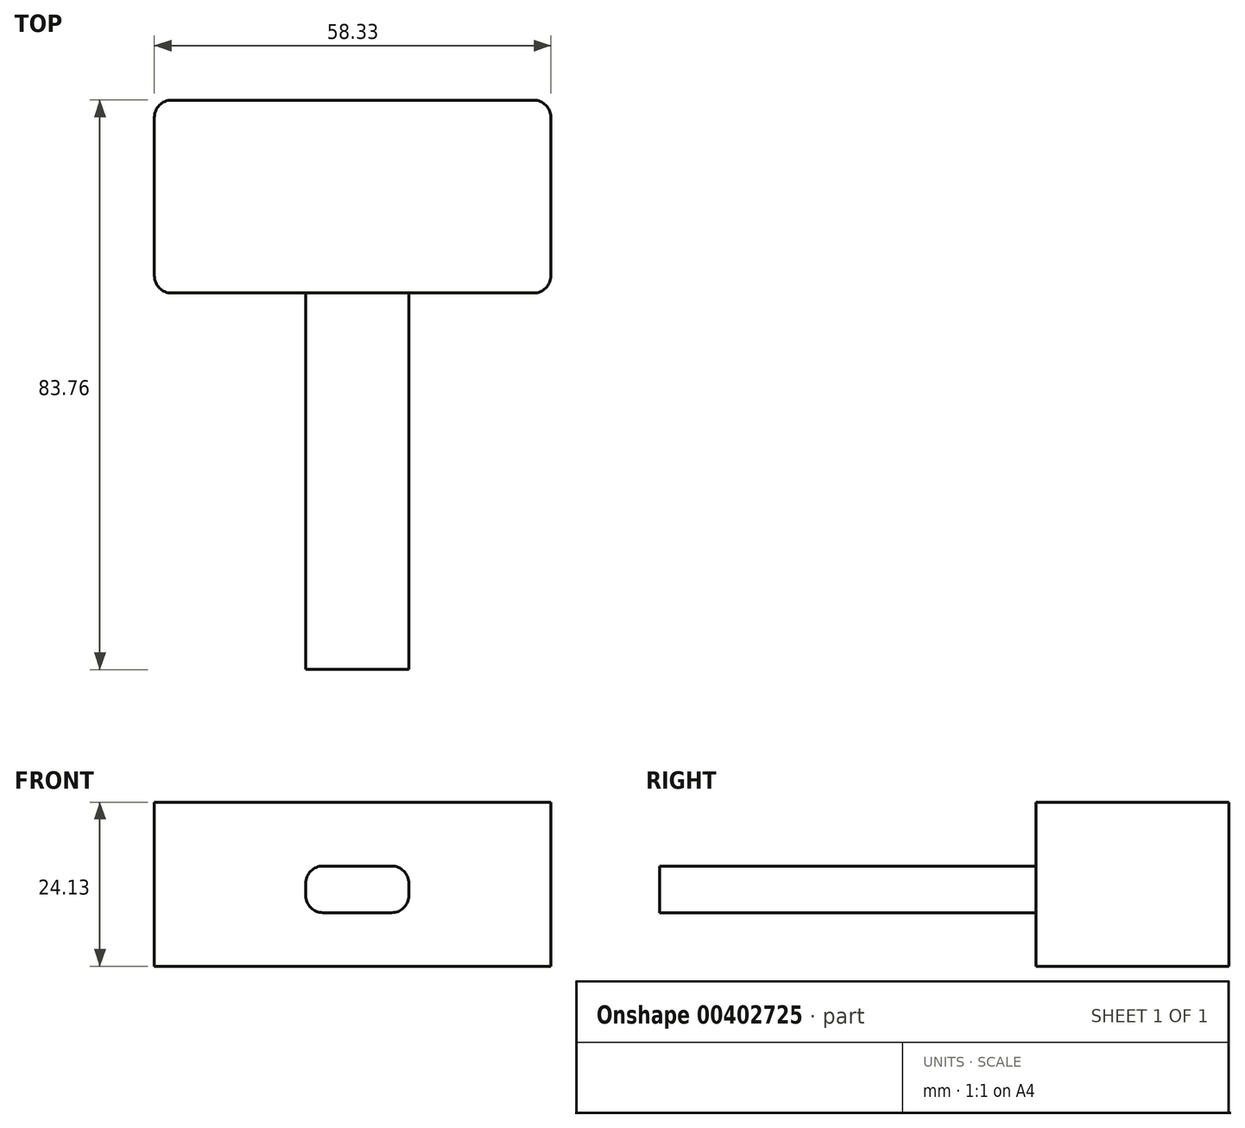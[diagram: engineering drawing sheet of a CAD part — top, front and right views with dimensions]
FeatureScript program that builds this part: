
annotation { "Feature Type Name" : "Feature", "Feature Type Description" : "" }
export const myFeature = defineFeature(function(context is Context, id is Id, definition is map)
    precondition{}
    {
        {
            var Q0;
            Q0=qCreatedBy(makeId("Top.planeOp"),FACE);
            var sketch = newSketch(context, id + "F0", { "sketchPlane" : qUnion([Q0])});
            skLineSegment(sketch, "E0.bottom", {"start": v(-8.47, 0) * mm, "end": v(6.7, 0) * mm});
            skLineSegment(sketch, "E0.top", {"start": v(-8.47, -55.38) * mm, "end": v(6.7, -55.38) * mm});
            skLineSegment(sketch, "E0.left", {"start": v(-8.47, 0) * mm, "end": v(-8.47, -55.38) * mm});
            skLineSegment(sketch, "E0.right", {"start": v(6.7, 0) * mm, "end": v(6.7, -55.38) * mm});
            skLineSegment(sketch, "E1.bottom", {"start": v(-30.74, 0) * mm, "end": v(27.59, 0) * mm});
            skLineSegment(sketch, "E1.top", {"start": v(-30.74, 28.38) * mm, "end": v(27.59, 28.38) * mm});
            skLineSegment(sketch, "E1.left", {"start": v(-30.74, 0) * mm, "end": v(-30.74, 28.38) * mm});
            skLineSegment(sketch, "E1.right", {"start": v(27.59, 0) * mm, "end": v(27.59, 28.38) * mm});
            skSolve(sketch);
        }
        {
            var Q0;
            Q0=makeQuery(id+"F0.imprint","IMPRINT",FACE,{"disambiguationData":[TD([[makeQuery(id+"F0.imprint","IMPRINT",EDGE,{"derivedFrom":sQuery(id+"F0.wireOp",EDGE,"E0.top")}),1.0]])]});
            extrude(context, id + "F1", {"entities" : qUnion([Q0]), "depth" : 6.35 * mm});
        }
        {
            var Q0;
            Q0=makeQuery(id+"F0.imprint","IMPRINT",FACE,{"disambiguationData":[TD([[makeQuery(id+"F0.imprint","IMPRINT",EDGE,{"derivedFrom":sQuery(id+"F0.wireOp",EDGE,"E1.top")}),-1.0]])]});
            extrude(context, id + "F2", {"entities" : qUnion([Q0]), "operationType" : NewBodyOperationType.ADD, "depth" : 16.26 * mm});
        }
        {
            var Q0;
            Q0=makeQuery(id+"F1.opExtrude","CAP_FACE",FACE,{"disambiguationData":[OSD([sQuery(id+"F0.wireOp",EDGE,"E0.top"),sQuery(id+"F0.wireOp",EDGE,"E0.left"),sQuery(id+"F0.wireOp",EDGE,"E0.right"),sQuery(id+"F0.wireOp",EDGE,"E1.bottom")])],"isStart":false});
            extrude(context, id + "F3", {"entities" : qUnion([Q0]), "operationType" : NewBodyOperationType.ADD, "depth" : 0.5 * mm});
        }
        {
            var Q0;
            Q0=makeQuery(id+"F0.imprint","IMPRINT",FACE,{"disambiguationData":[TD([[makeQuery(id+"F0.imprint","IMPRINT",EDGE,{"derivedFrom":sQuery(id+"F0.wireOp",EDGE,"E1.top")}),-1.0]])]});
            extrude(context, id + "F4", {"entities" : qUnion([Q0]), "operationType" : NewBodyOperationType.ADD, "oppositeDirection" : true, "depth" : 7.87 * mm});
        }
        {
            var Q0;
            Q0=makeQuery(id+"F1.opExtrude","CAP_EDGE",EDGE,{"disambiguationData":[OSD([sQuery(id+"F0.wireOp",EDGE,"E0.left")])],"isStart":true});
            var Q1;
            Q1=makeQuery(id+"F3.opExtrude","CAP_EDGE",EDGE,{"disambiguationData":[OSD([sQuery(id+"F0.wireOp",EDGE,"E0.left")])],"isStart":false});
            var Q2;
            Q2=makeQuery(id+"F3.opExtrude","CAP_EDGE",EDGE,{"disambiguationData":[OSD([sQuery(id+"F0.wireOp",EDGE,"E0.right")])],"isStart":false});
            var Q3;
            Q3=makeQuery(id+"F1.opExtrude","CAP_EDGE",EDGE,{"disambiguationData":[OSD([sQuery(id+"F0.wireOp",EDGE,"E0.right")])],"isStart":true});
            var Q4;
            {var subQ0=sQuery(id+"F0.wireOp",EDGE,"E1.right");var subQ1=sQuery(id+"F0.wireOp",EDGE,"E1.bottom");Q4=makeQuery(id+"F4.boolean.opBoolean","MERGE",EDGE,{"derivedFrom":[makeQuery(id+"F2.opExtrude","SWEPT_EDGE",EDGE,{"disambiguationData":[OSD([subQ1,subQ0])]}),makeQuery(id+"F4.opExtrude","SWEPT_EDGE",EDGE,{"disambiguationData":[OSD([subQ1,subQ0])]})]});}
            var Q5;
            {var subQ0=sQuery(id+"F0.wireOp",EDGE,"E1.left");var subQ1=sQuery(id+"F0.wireOp",EDGE,"E1.bottom");Q5=makeQuery(id+"F4.boolean.opBoolean","MERGE",EDGE,{"derivedFrom":[makeQuery(id+"F2.opExtrude","SWEPT_EDGE",EDGE,{"disambiguationData":[OSD([subQ1,subQ0])]}),makeQuery(id+"F4.opExtrude","SWEPT_EDGE",EDGE,{"disambiguationData":[OSD([subQ1,subQ0])]})]});}
            var Q6;
            {var subQ0=sQuery(id+"F0.wireOp",EDGE,"E1.left");var subQ1=sQuery(id+"F0.wireOp",EDGE,"E1.top");Q6=makeQuery(id+"F4.boolean.opBoolean","MERGE",EDGE,{"derivedFrom":[makeQuery(id+"F2.opExtrude","SWEPT_EDGE",EDGE,{"disambiguationData":[OSD([subQ1,subQ0])]}),makeQuery(id+"F4.opExtrude","SWEPT_EDGE",EDGE,{"disambiguationData":[OSD([subQ1,subQ0])]})]});}
            var Q7;
            {var subQ0=sQuery(id+"F0.wireOp",EDGE,"E1.right");var subQ1=sQuery(id+"F0.wireOp",EDGE,"E1.top");Q7=makeQuery(id+"F4.boolean.opBoolean","MERGE",EDGE,{"derivedFrom":[makeQuery(id+"F2.opExtrude","SWEPT_EDGE",EDGE,{"disambiguationData":[OSD([subQ1,subQ0])]}),makeQuery(id+"F4.opExtrude","SWEPT_EDGE",EDGE,{"disambiguationData":[OSD([subQ1,subQ0])]})]});}
            fillet(context, id + "F5", {"entities" : qUnion([Q0, Q1, Q2, Q3, Q4, Q5, Q6, Q7]), "radius" : 2.54 * mm, "tangentPropagation" : true, "allowEdgeOverflow" : false});
        }
    });
